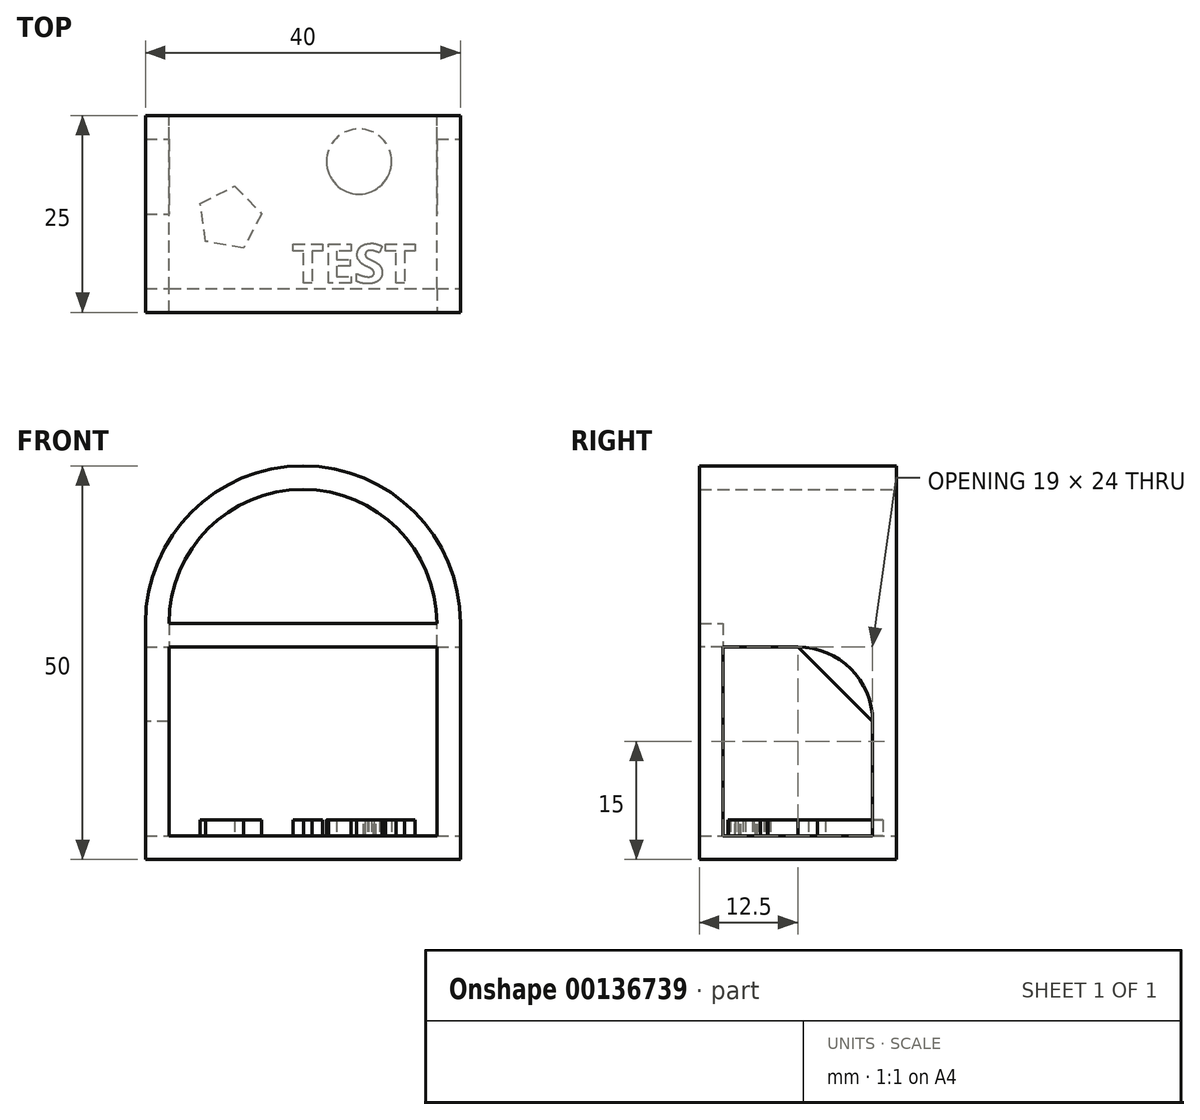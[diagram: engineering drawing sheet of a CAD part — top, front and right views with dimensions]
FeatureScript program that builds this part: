
annotation { "Feature Type Name" : "Feature", "Feature Type Description" : "" }
export const myFeature = defineFeature(function(context is Context, id is Id, definition is map)
    precondition{}
    {
        {
            var Q0;
            Q0=qCreatedBy(makeId("Front.planeOp"),FACE);
            var sketch = newSketch(context, id + "F0", { "sketchPlane" : qUnion([Q0])});
            skLineSegment(sketch, "E0.top", {"start": v(20, -15) * mm, "end": v(-20, -15) * mm});
            skLineSegment(sketch, "E0.left", {"start": v(20, 15) * mm, "end": v(20, -15) * mm});
            skLineSegment(sketch, "E0.right", {"start": v(-20, 15) * mm, "end": v(-20, -15) * mm});
            skPoint(sketch, "E0.middle", {"position": v(0, 0) * mm});
            skArc(sketch, "E1", {"start": v(20, 15) * mm, "mid": v(0, 35) * mm, "end": v(-20, 15) * mm});
            skLineSegment(sketch, "E2.0", {"start": v(17, 15) * mm, "end": v(17, -12) * mm});
            skArc(sketch, "E2.1", {"start": v(17, 15) * mm, "mid": v(0, 32) * mm, "end": v(-17, 15) * mm});
            skLineSegment(sketch, "E2.2", {"start": v(-17, 15) * mm, "end": v(-17, -12) * mm});
            skLineSegment(sketch, "E2.3", {"start": v(17, -12) * mm, "end": v(-17, -12) * mm});
            skSolve(sketch);
        }
        {
            var Q0;
            Q0=makeQuery(id+"F0.imprint","IMPRINT",FACE,{"disambiguationData":[TD([[makeQuery(id+"F0.imprint","IMPRINT",EDGE,{"derivedFrom":sQuery(id+"F0.wireOp",EDGE,"E0.top")}),-1.0]])]});
            extrude(context, id + "F1", {"entities" : qUnion([Q0]), "depth" : 25 * mm});
        }
        {
            var Q0;
            Q0=makeQuery(id+"F1.opExtrude","SWEPT_FACE",FACE,{"disambiguationData":[OSD([sQuery(id+"F0.wireOp",EDGE,"E0.left")])]});
            var sketch = newSketch(context, id + "F2", { "sketchPlane" : qUnion([Q0])});
            skLineSegment(sketch, "E3", {"start": v(-3, -12) * mm, "end": v(-22, -12) * mm});
            skLineSegment(sketch, "E4", {"start": v(-22, -12) * mm, "end": v(-22, 12) * mm});
            skLineSegment(sketch, "E5", {"start": v(-22, 12) * mm, "end": v(-3, 12) * mm});
            skLineSegment(sketch, "E6", {"start": v(-3, 12) * mm, "end": v(-3, -12) * mm});
            skSolve(sketch);
        }
        {
            var Q0;
            Q0=makeQuery(id+"F2.imprint","IMPRINT",FACE,{"disambiguationData":[TD([[makeQuery(id+"F2.imprint","IMPRINT",EDGE,{"derivedFrom":sQuery(id+"F2.wireOp",EDGE,"E3")}),-1.0]])]});
            extrude(context, id + "F3", {"entities" : qUnion([Q0]), "operationType" : NewBodyOperationType.REMOVE, "endBound" : BoundingType.THROUGH_ALL, "oppositeDirection" : true, "depth" : 25 * mm});
        }
        {
            var Q0;
            {var subQ0=sQuery(id+"F2.wireOp",EDGE,"E5");var subQ1=sQuery(id+"F2.wireOp",EDGE,"E6");Q0=makeQuery(id+"F3.boolean.opBoolean","COPY",EDGE,{"disambiguationData":[TD([makeQuery(id+"F1.opExtrude","SWEPT_FACE",FACE,{"disambiguationData":[OSD([sQuery(id+"F0.wireOp",EDGE,"E0.right")])]})])],"derivedFrom":makeQuery(id+"F3.opExtrude","SWEPT_EDGE",EDGE,{"disambiguationData":[OSD([subQ0,subQ1])]})});}
            chamfer(context, id + "F4", {"entities" : qUnion([Q0]), "width" : 9.5 * mm, "tangentPropagation" : true});
        }
        {
            var Q0;
            {var subQ0=sQuery(id+"F2.wireOp",EDGE,"E5");var subQ1=sQuery(id+"F2.wireOp",EDGE,"E6");Q0=makeQuery(id+"F3.boolean.opBoolean","COPY",EDGE,{"disambiguationData":[TD([makeQuery(id+"F1.opExtrude","SWEPT_FACE",FACE,{"disambiguationData":[OSD([sQuery(id+"F0.wireOp",EDGE,"E0.left")])]})])],"derivedFrom":makeQuery(id+"F3.opExtrude","SWEPT_EDGE",EDGE,{"disambiguationData":[OSD([subQ0,subQ1])]})});}
            fillet(context, id + "F5", {"entities" : qUnion([Q0]), "radius" : 9.5 * mm, "tangentPropagation" : true, "allowEdgeOverflow" : false});
        }
        {
            var Q0;
            Q0=makeQuery(id+"F1.opExtrude","SWEPT_FACE",FACE,{"disambiguationData":[OSD([sQuery(id+"F0.wireOp",EDGE,"E0.left")])]});
            var sketch = newSketch(context, id + "F6", { "sketchPlane" : qUnion([Q0])});
            skLineSegment(sketch, "E7.bottom", {"start": v(-22, 12) * mm, "end": v(-25, 12) * mm});
            skLineSegment(sketch, "E7.top", {"start": v(-22, 15) * mm, "end": v(-25, 15) * mm});
            skLineSegment(sketch, "E7.left", {"start": v(-22, 12) * mm, "end": v(-22, 15) * mm});
            skLineSegment(sketch, "E7.right", {"start": v(-25, 12) * mm, "end": v(-25, 15) * mm});
            skSolve(sketch);
        }
        {
            var Q0;
            Q0=makeQuery(id+"F6.imprint","IMPRINT",FACE,{"disambiguationData":[TD([[makeQuery(id+"F6.imprint","IMPRINT",EDGE,{"derivedFrom":sQuery(id+"F6.wireOp",EDGE,"E7.bottom")}),-1.0]])]});
            var Q1;
            Q1=makeQuery(id+"F1.opExtrude","SWEPT_FACE",FACE,{"disambiguationData":[OSD([sQuery(id+"F0.wireOp",EDGE,"E2.2")])]});
            extrude(context, id + "F7", {"entities" : qUnion([Q0]), "operationType" : NewBodyOperationType.ADD, "endBound" : BoundingType.UP_TO_SURFACE, "oppositeDirection" : true, "endBoundEntityFace" : qUnion([Q1]), "depth" : 25 * mm});
        }
        {
            var Q0;
            Q0=makeQuery(id+"F3.boolean.opBoolean","MERGE",FACE,{"derivedFrom":[makeQuery(id+"F1.opExtrude","SWEPT_FACE",FACE,{"disambiguationData":[OSD([sQuery(id+"F0.wireOp",EDGE,"E2.3")])]}),makeQuery(id+"F3.opExtrude","SWEPT_FACE",FACE,{"disambiguationData":[OSD([sQuery(id+"F2.wireOp",EDGE,"E3")])]})]});
            var sketch = newSketch(context, id + "F8", { "sketchPlane" : qUnion([Q0])});
            skCircle(sketch, "E8.cCircle", {"center": v(-9.37, -13.1) * mm, "radius": 3.36 * mm, "construction": true});
            skLineSegment(sketch, "E8.0", {"start": v(-8.66, -9) * mm, "end": v(-5.25, -12.5) * mm});
            skLineSegment(sketch, "E8.1", {"start": v(-5.25, -12.5) * mm, "end": v(-7.53, -16.82) * mm});
            skLineSegment(sketch, "E8.2", {"start": v(-7.53, -16.82) * mm, "end": v(-12.34, -16) * mm});
            skLineSegment(sketch, "E8.3", {"start": v(-12.34, -16) * mm, "end": v(-13.05, -11.16) * mm});
            skLineSegment(sketch, "E8.4", {"start": v(-13.05, -11.16) * mm, "end": v(-8.66, -9) * mm});
            skPoint(sketch, "E8.0.midPoint", {"position": v(-6.96, -10.74) * mm});
            skCircle(sketch, "E9", {"center": v(7.12, -5.84) * mm, "radius": 4.14 * mm});
            skText(sketch, "E10", { "text": "TEST", "fontName": "OpenSans-Bold.ttf"});
            const initialGuessF8  = {"E10": [-0.0014, -0.0213, 1, 0, 0.005]};
            skSetInitialGuess(sketch, initialGuessF8);
            skSolve(sketch);
        }
        {
            var Q0;
            Q0=makeQuery(id+"F8.imprint","IMPRINT",FACE,{"disambiguationData":[TD([[makeQuery(id+"F8.imprint","IMPRINT",EDGE,{"derivedFrom":sQuery(id+"F8.wireOp",EDGE,"E8.0")}),-1.0]])]});
            var Q1;
            Q1=makeQuery(id+"F8.imprint","IMPRINT",FACE,{"disambiguationData":[TD([[makeQuery(id+"F8.imprint","IMPRINT",EDGE,{"derivedFrom":sQuery(id+"F8.wireOp",EDGE,"E9")}),1.0]])]});
            var Q2;
            Q2=makeQuery(id+"F8.imprint","IMPRINT",FACE,{"disambiguationData":[TD([[makeQuery(id+"F8.imprint","IMPRINT",EDGE,{"derivedFrom":sQuery(id+"F8.wireOp",EDGE,"E10.sketch_text.stroke-0")}),-1.0]])]});
            var Q3;
            Q3=makeQuery(id+"F8.imprint","IMPRINT",FACE,{"disambiguationData":[TD([[makeQuery(id+"F8.imprint","IMPRINT",EDGE,{"derivedFrom":sQuery(id+"F8.wireOp",EDGE,"E10.sketch_text.stroke-8")}),-1.0]])]});
            var Q4;
            Q4=makeQuery(id+"F8.imprint","IMPRINT",FACE,{"disambiguationData":[TD([[makeQuery(id+"F8.imprint","IMPRINT",EDGE,{"derivedFrom":sQuery(id+"F8.wireOp",EDGE,"E10.sketch_text.stroke-20")}),-1.0]])]});
            var Q5;
            Q5=makeQuery(id+"F8.imprint","IMPRINT",FACE,{"disambiguationData":[TD([[makeQuery(id+"F8.imprint","IMPRINT",EDGE,{"derivedFrom":sQuery(id+"F8.wireOp",EDGE,"E10.sketch_text.stroke-48")}),-1.0]])]});
            extrude(context, id + "F9", {"entities" : qUnion([Q0, Q1, Q2, Q3, Q4, Q5]), "operationType" : NewBodyOperationType.ADD, "depth" : 2 * mm});
        }
    });
